# Revit family: Power-ModularDevices-GEWISS-90AM-CONTACTORS_25A
name_source: partatom
category: Apparecchi elettrici
revit_build: Autodesk Revit 2016 (Build: 20161004_0715(x64)
units: mm (PartAtom-declared; Revit-internal decimal feet)

## family parameters
Condiviso = No
Host = Superficie
Mantenere orientamento annotazione = Sì
Numero OmniClass = 23.80.30.00
Punto di calcolo locali = Sì
Quota connettore circolare = Usa diametro
Taglio con vuoti quando caricato = No
Tipo di parte = Normale
Titolo OmniClass = Distribution Devices

## types (8) — shared parameters
A = 36 mm  [stored 0.11811 ft]
B = 85 mm  [stored 0.278871 ft]
C = 65 mm  [stored 0.213255 ft]
Catalogue = POWER
Catalogue Range = 90 AM
D = 45 mm  [stored 0.147638 ft]
Electrocod = 1712
Fin_contattore = <Per categoria>
IDF = e388ba80-26c5-4a98-97bc-c528305914bb
IDT = 92cc9d4e-eaa0-4e49-bd7b-0148e15aca92
Immagine tipo = GWD6718.jpg
No. Chorus modules = 2
Numero poli = 1
Potenza in Watt = 0 V
Produttore = GEWISS S.p.A.
Prospetto di default = 1219 mm
Rated current (AC-1/AC-7a) = 25 A - CTR25
TEXT LABEL = A
Technical sheet = https://www.gewiss.com
URL = https://www.gewiss.com
Version file RFA = 18.0

## per-type parameters (varying)
| type | Control coil voltage (V) | Descrizione | EAN code | Modello |
| GWD6712 - CONTACTOR 25A 2NO 230V 2M | 230Vac - 220Vdc | CONTACTOR 25A 2NO 230V 2M | 8011564809468 | GWD6712 |
| GWD6716 - CONTACTOR 25A 4NC 24V 2M | 24Vac/dc | CONTACTOR 25A 4NC 24V 2M | 8011564809505 | GWD6716 |
| GWD6713 - CONTACTOR 25A 3NO 230V 2M | 230Vac - 220Vdc | CONTACTOR 25A 3NO 230V 2M | 8011564809475 | GWD6713 |
| GWD6711 - CONTACTOR 25A 2NO 24V 2M | 24Vac/dc | CONTACTOR 25A 2NO 24V 2M | 8011564809451 | GWD6711 |
| GWD6715 - CONTACTOR 25A 4NO 230V 2M | 230Vac - 220Vdc | CONTACTOR 25A 4NO 230V 2M | 8011564809499 | GWD6715 |
| GWD6717 - CONTACTOR 25A 4NC 230V 2M | 230Vac - 220Vdc | CONTACTOR 25A 4NC 230V 2M | 8011564809512 | GWD6717 |
| GWD6718 - CONTACTOR 25A 3NO+1NC 230V 2M | 230Vac - 220Vdc | CONTACTOR 25A 3NO+1NC 230V 2M | 8011564809529 | GWD6718 |
| GWD6714 - CONTACTOR 25A 4NO 24V 2M | 24Vac/dc | CONTACTOR 25A 4NO 24V 2M | 8011564809482 | GWD6714 |

note: [stored X ft] marks values corroborated as IEEE doubles in the binary element streams (Revit-internal decimal feet)
